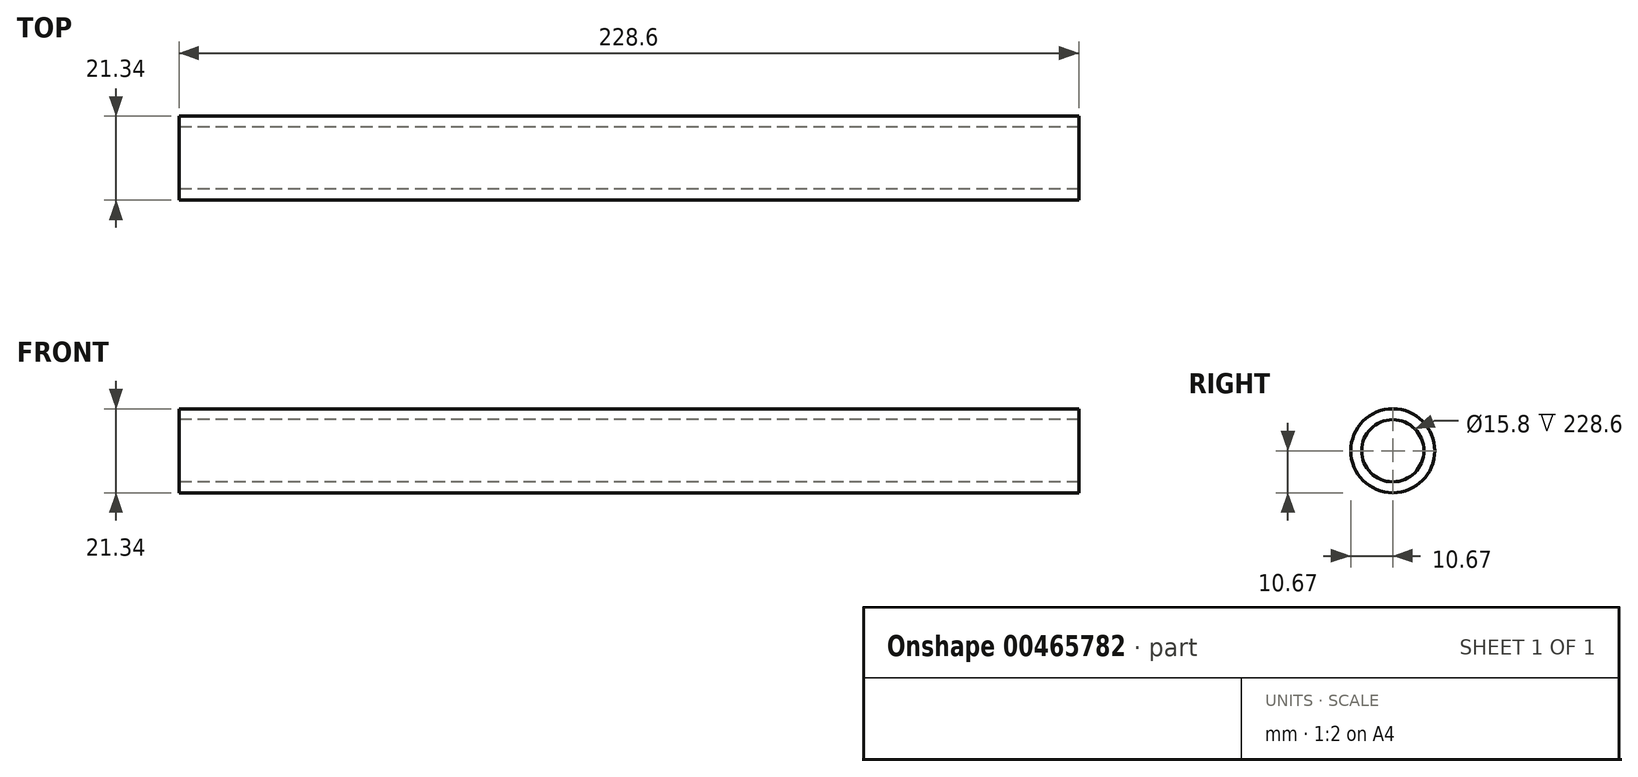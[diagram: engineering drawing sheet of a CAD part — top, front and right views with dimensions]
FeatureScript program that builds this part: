
annotation { "Feature Type Name" : "Feature", "Feature Type Description" : "" }
export const myFeature = defineFeature(function(context is Context, id is Id, definition is map)
    precondition{}
    {
        {
            var Q0;
            Q0=qCreatedBy(makeId("Right.planeOp"),FACE);
            var sketch = newSketch(context, id + "F0", { "sketchPlane" : qUnion([Q0])});
            skCircle(sketch, "E0", {"center": v(0, 0) * mm, "radius": 10.67 * mm});
            skCircle(sketch, "E1", {"center": v(0, 0) * mm, "radius": 7.9 * mm});
            skSolve(sketch);
        }
        {
            var Q0;
            Q0=makeQuery(id+"F0.imprint","IMPRINT",FACE,{"disambiguationData":[TD([[makeQuery(id+"F0.imprint","IMPRINT",EDGE,{"derivedFrom":sQuery(id+"F0.wireOp",EDGE,"E0")}),1.0]])]});
            extrude(context, id + "F1", {"entities" : qUnion([Q0]), "endBound" : BoundingType.SYMMETRIC, "depth" : 228.6 * mm});
        }
    });
